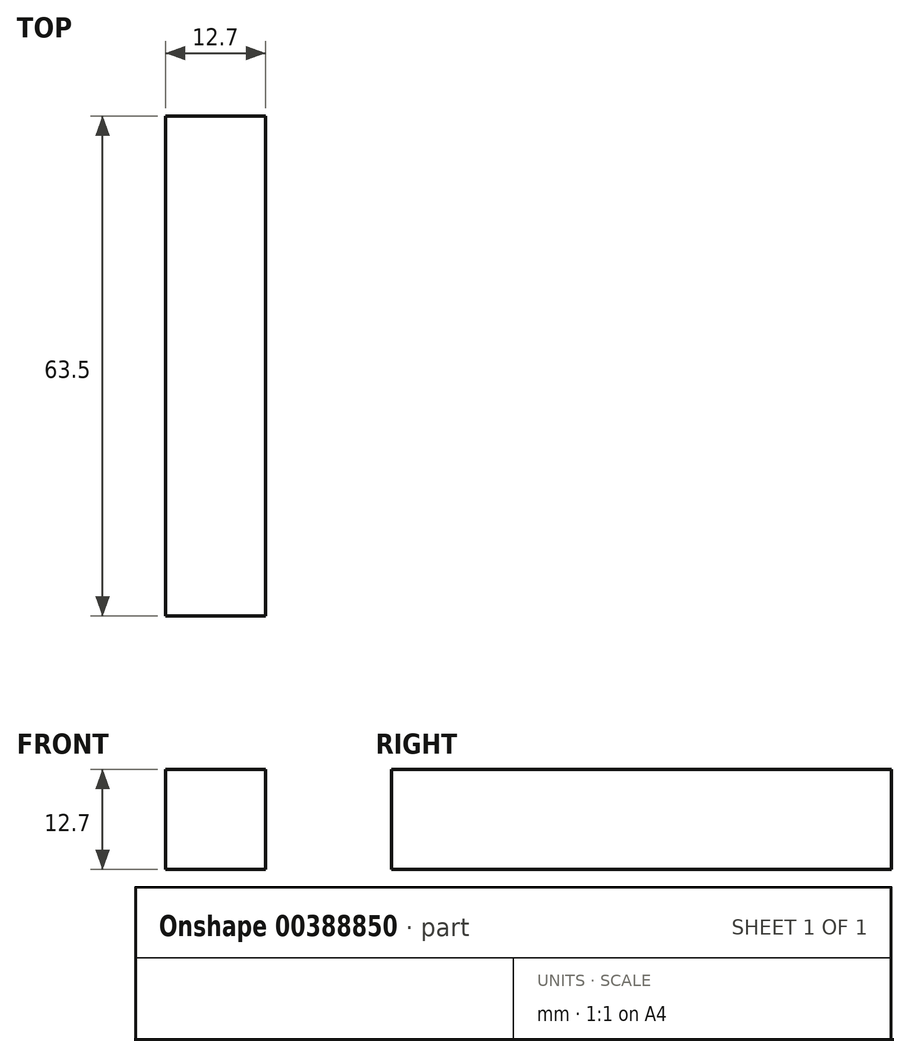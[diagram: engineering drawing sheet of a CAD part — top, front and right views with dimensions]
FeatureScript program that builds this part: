
annotation { "Feature Type Name" : "Feature", "Feature Type Description" : "" }
export const myFeature = defineFeature(function(context is Context, id is Id, definition is map)
    precondition{}
    {
        {
            var Q0;
            Q0=qCreatedBy(makeId("Top.planeOp"),FACE);
            var sketch = newSketch(context, id + "F0", { "sketchPlane" : qUnion([Q0])});
            skLineSegment(sketch, "E0.bottom", {"start": v(0, 0) * mm, "end": v(12.7, 0) * mm});
            skLineSegment(sketch, "E0.top", {"start": v(0, 63.5) * mm, "end": v(12.7, 63.5) * mm});
            skLineSegment(sketch, "E0.left", {"start": v(0, 0) * mm, "end": v(0, 63.5) * mm});
            skLineSegment(sketch, "E0.right", {"start": v(12.7, 0) * mm, "end": v(12.7, 63.5) * mm});
            skSolve(sketch);
        }
        {
            var Q0;
            Q0=makeQuery(id+"F0.imprint","IMPRINT",FACE,{"disambiguationData":[TD([[makeQuery(id+"F0.imprint","IMPRINT",EDGE,{"derivedFrom":sQuery(id+"F0.wireOp",EDGE,"E0.bottom")}),1.0]])]});
            extrude(context, id + "F1", {"entities" : qUnion([Q0]), "depth" : 12.7 * mm});
        }
    });
